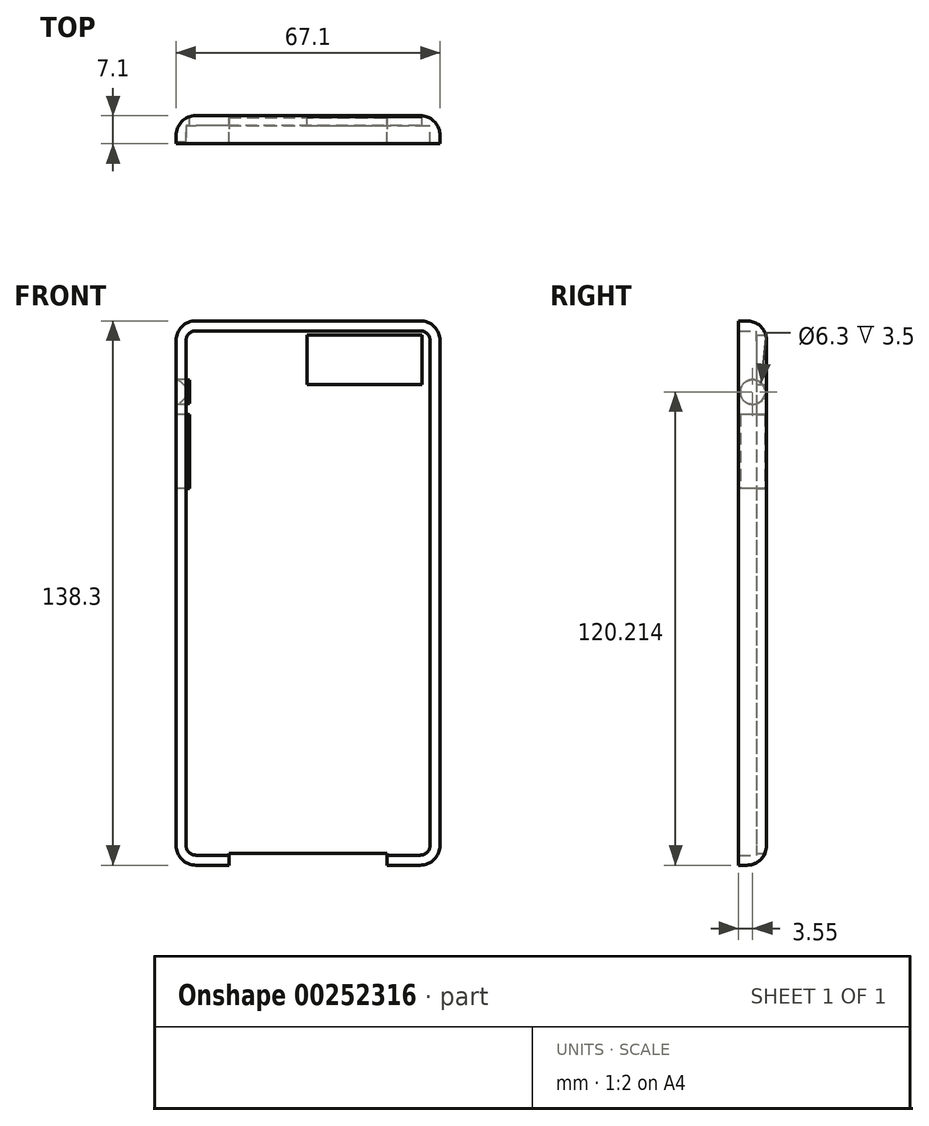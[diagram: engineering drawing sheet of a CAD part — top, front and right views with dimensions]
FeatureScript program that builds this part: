
annotation { "Feature Type Name" : "Feature", "Feature Type Description" : "" }
export const myFeature = defineFeature(function(context is Context, id is Id, definition is map)
    precondition{}
    {
        {
            var Q0;
            Q0=qCreatedBy(makeId("Front.planeOp"),FACE);
            var sketch = newSketch(context, id + "F0", { "sketchPlane" : qUnion([Q0])});
            skLineSegment(sketch, "E0.bottom", {"start": v(33.55, 69.15) * mm, "end": v(-33.55, 69.15) * mm});
            skLineSegment(sketch, "E0.top", {"start": v(33.55, -69.15) * mm, "end": v(-33.55, -69.15) * mm});
            skLineSegment(sketch, "E0.left", {"start": v(33.55, 69.15) * mm, "end": v(33.55, -69.15) * mm});
            skLineSegment(sketch, "E0.right", {"start": v(-33.55, 69.15) * mm, "end": v(-33.55, -69.15) * mm});
            skPoint(sketch, "E0.middle", {"position": v(0, 0) * mm});
            skSolve(sketch);
        }
        {
            var Q0;
            Q0=makeQuery(id+"F0.imprint","IMPRINT",FACE,{"disambiguationData":[TD([[makeQuery(id+"F0.imprint","IMPRINT",EDGE,{"derivedFrom":sQuery(id+"F0.wireOp",EDGE,"E0.bottom")}),1.0]])]});
            extrude(context, id + "F1", {"entities" : qUnion([Q0]), "endBound" : BoundingType.SYMMETRIC, "depth" : 7.1 * mm});
        }
        {
            var Q0;
            Q0=makeQuery(id+"F1.opExtrude","SWEPT_EDGE",EDGE,{"disambiguationData":[OSD([sQuery(id+"F0.wireOp",EDGE,"E0.bottom"),sQuery(id+"F0.wireOp",EDGE,"E0.right")])]});
            var Q1;
            Q1=makeQuery(id+"F1.opExtrude","SWEPT_EDGE",EDGE,{"disambiguationData":[OSD([sQuery(id+"F0.wireOp",EDGE,"E0.bottom"),sQuery(id+"F0.wireOp",EDGE,"E0.left")])]});
            var Q2;
            Q2=makeQuery(id+"F1.opExtrude","SWEPT_EDGE",EDGE,{"disambiguationData":[OSD([sQuery(id+"F0.wireOp",EDGE,"E0.top"),sQuery(id+"F0.wireOp",EDGE,"E0.left")])]});
            var Q3;
            Q3=makeQuery(id+"F1.opExtrude","SWEPT_EDGE",EDGE,{"disambiguationData":[OSD([sQuery(id+"F0.wireOp",EDGE,"E0.top"),sQuery(id+"F0.wireOp",EDGE,"E0.right")])]});
            fillet(context, id + "F2", {"entities" : qUnion([Q0, Q1, Q2, Q3]), "radius" : 5.08 * mm, "tangentPropagation" : true, "allowEdgeOverflow" : false});
        }
        {
            var Q0;
            Q0=makeQuery(id+"F1.opExtrude","CAP_FACE",FACE,{"disambiguationData":[OSD([sQuery(id+"F0.wireOp",EDGE,"E0.bottom"),sQuery(id+"F0.wireOp",EDGE,"E0.top"),sQuery(id+"F0.wireOp",EDGE,"E0.left"),sQuery(id+"F0.wireOp",EDGE,"E0.right")])],"isStart":false});
            shell(context, id + "F3", {"entities" : qUnion([Q0]), "thickness" : 2.54 * mm});
        }
        {
            var Q0;
            Q0=qCreatedBy(makeId("Front.planeOp"),FACE);
            var sketch = newSketch(context, id + "F4", { "sketchPlane" : qUnion([Q0])});
            skLineSegment(sketch, "E1.bottom", {"start": v(28.98, 52.93) * mm, "end": v(-0.29, 52.93) * mm});
            skLineSegment(sketch, "E1.top", {"start": v(28.98, 65.55) * mm, "end": v(-0.29, 65.55) * mm});
            skLineSegment(sketch, "E1.left", {"start": v(28.98, 52.93) * mm, "end": v(28.98, 65.55) * mm});
            skLineSegment(sketch, "E1.right", {"start": v(-0.29, 52.93) * mm, "end": v(-0.29, 65.55) * mm});
            skPoint(sketch, "E1.middle", {"position": v(14.34, 59.24) * mm});
            skSolve(sketch);
        }
        {
            var Q0;
            Q0=makeQuery(id+"F4.imprint","IMPRINT",FACE,{"disambiguationData":[TD([[makeQuery(id+"F4.imprint","IMPRINT",EDGE,{"derivedFrom":sQuery(id+"F4.wireOp",EDGE,"E1.bottom")}),-1.0]])]});
            extrude(context, id + "F5", {"entities" : qUnion([Q0]), "operationType" : NewBodyOperationType.REMOVE, "endBound" : BoundingType.SYMMETRIC, "depth" : 25 * mm});
        }
        {
            var Q0;
            Q0=makeQuery(id+"F1.opExtrude","SWEPT_FACE",FACE,{"disambiguationData":[OSD([sQuery(id+"F0.wireOp",EDGE,"E0.top")])]});
            var sketch = newSketch(context, id + "F6", { "sketchPlane" : qUnion([Q0])});
            skLineSegment(sketch, "E2.bottom", {"start": v(-20.08, 3.55) * mm, "end": v(20.08, 3.55) * mm});
            skLineSegment(sketch, "E2.top", {"start": v(-20.08, -3.55) * mm, "end": v(20.08, -3.55) * mm});
            skLineSegment(sketch, "E2.left", {"start": v(-20.08, 3.55) * mm, "end": v(-20.08, -3.55) * mm});
            skLineSegment(sketch, "E2.right", {"start": v(20.08, 3.55) * mm, "end": v(20.08, -3.55) * mm});
            skPoint(sketch, "E2.middle", {"position": v(0, 0) * mm});
            skSolve(sketch);
        }
        {
            var Q0;
            Q0 = qSketchRegion(id + "F6", true);
            extrude(context, id + "F7", {"entities" : qUnion([Q0]), "operationType" : NewBodyOperationType.REMOVE, "endBound" : BoundingType.SYMMETRIC, "oppositeDirection" : true, "depth" : 6 * mm});
        }
        {
            var Q0;
            Q0=makeQuery(id+"F1.opExtrude","SWEPT_FACE",FACE,{"disambiguationData":[OSD([sQuery(id+"F0.wireOp",EDGE,"E0.right")])]});
            var sketch = newSketch(context, id + "F8", { "sketchPlane" : qUnion([Q0])});
            skCircle(sketch, "E3", {"center": v(0, 51.06) * mm, "radius": 3.15 * mm});
            skSolve(sketch);
        }
        {
            var Q0;
            Q0=makeQuery(id+"F8.imprint","IMPRINT",FACE,{"disambiguationData":[TD([[makeQuery(id+"F8.imprint","IMPRINT",EDGE,{"derivedFrom":sQuery(id+"F8.wireOp",EDGE,"E3")}),1.0]])]});
            extrude(context, id + "F9", {"entities" : qUnion([Q0]), "operationType" : NewBodyOperationType.REMOVE, "endBound" : BoundingType.SYMMETRIC, "oppositeDirection" : true, "depth" : 7 * mm});
        }
        {
            var Q0;
            Q0=makeQuery(id+"F1.opExtrude","SWEPT_FACE",FACE,{"disambiguationData":[OSD([sQuery(id+"F0.wireOp",EDGE,"E0.right")])]});
            var sketch = newSketch(context, id + "F10", { "sketchPlane" : qUnion([Q0])});
            skLineSegment(sketch, "E4.bottom", {"start": v(3.09, 26.49) * mm, "end": v(-3.09, 26.49) * mm});
            skLineSegment(sketch, "E4.top", {"start": v(3.09, 45.3) * mm, "end": v(-3.09, 45.3) * mm});
            skLineSegment(sketch, "E4.left", {"start": v(3.09, 26.49) * mm, "end": v(3.09, 45.3) * mm});
            skLineSegment(sketch, "E4.right", {"start": v(-3.09, 26.49) * mm, "end": v(-3.09, 45.3) * mm});
            skPoint(sketch, "E4.middle", {"position": v(0, 35.9) * mm});
            skSolve(sketch);
        }
        {
            var Q0;
            Q0=makeQuery(id+"F10.imprint","IMPRINT",FACE,{"disambiguationData":[TD([[makeQuery(id+"F10.imprint","IMPRINT",EDGE,{"derivedFrom":sQuery(id+"F10.wireOp",EDGE,"E4.bottom")}),-1.0]])]});
            extrude(context, id + "F11", {"entities" : qUnion([Q0]), "operationType" : NewBodyOperationType.REMOVE, "endBound" : BoundingType.SYMMETRIC, "oppositeDirection" : true, "depth" : 7 * mm});
        }
        {
            var Q0;
            Q0=makeQuery(id+"F1.opExtrude","CAP_EDGE",EDGE,{"disambiguationData":[OSD([sQuery(id+"F0.wireOp",EDGE,"E0.left")])],"isStart":true});
            fillet(context, id + "F12", {"entities" : qUnion([Q0]), "radius" : 5 * mm, "tangentPropagation" : true, "allowEdgeOverflow" : false});
        }
    });
